# Revit family: Sense suihkuistuin
name_source: partatom
category: Casework
revit_build: Autodesk Revit 2015 (Build: 20140606_1530(x64)
units: mm (PartAtom-declared; Revit-internal decimal feet)

## types (6) — shared parameters
Depth = 518 mm  [stored 1.69948 ft]
Height = 835 mm
Manufacturer = Korpinen
Model = Sense suihkuistuin
URL = http://www.korpinen.com
Width = 426 mm  [stored 1.39764 ft]
zero-valued in all types: NominalDepth, NominalHeight, NominalLength

## per-type parameters (varying)
| type | Keynote | Shower seat |
| 17413 G | 17413 | Sense suihkuistuin 17413 : Sense suihkuistuin 17413 G |
| 17413 R | 17413 | Sense suihkuistuin 17413 : Sense suihkuistuin 17413 R |
| 17413 Y | 17413 | Sense suihkuistuin 17413 : Sense suihkuistuin 17413 Y |
| 17412 G | 17412 | Sense suihkuistuin 17412 : Sense suihkuistuin 17412 G |
| 17412 R | 17412 | Sense suihkuistuin 17412 : Sense suihkuistuin 17412 R |
| 17412 Y | 17412 | Sense suihkuistuin 17412 : Sense suihkuistuin 17412 Y |

note: [stored X ft] marks values corroborated as IEEE doubles in the binary element streams (Revit-internal decimal feet)

## geometry (parser evidence)
native form markers: Blend x10, Sweep x7
no freeform markers — native parametric forms only
